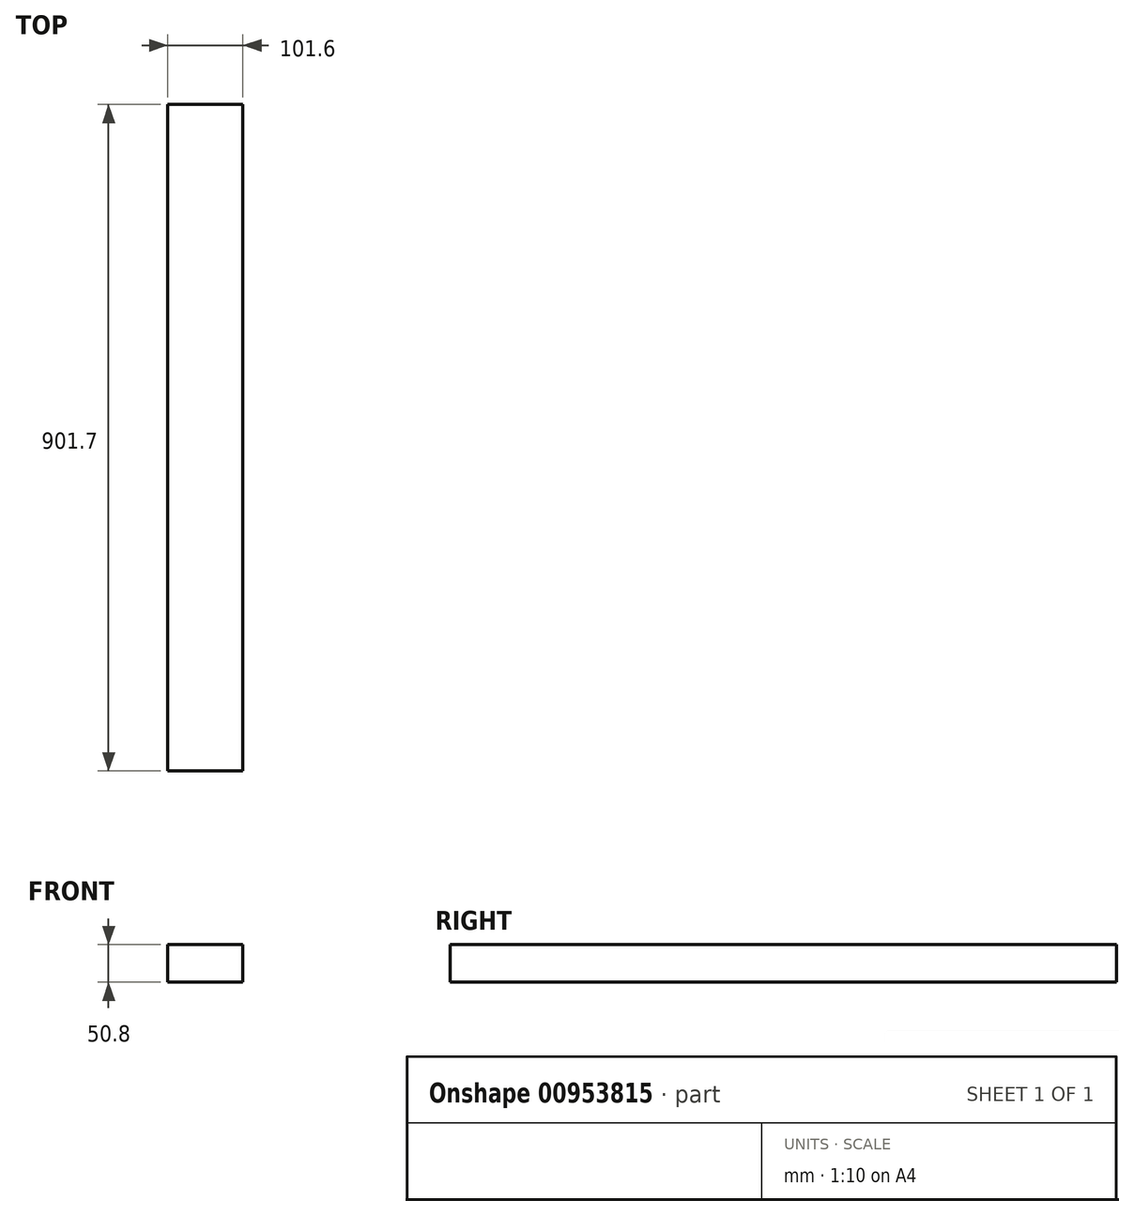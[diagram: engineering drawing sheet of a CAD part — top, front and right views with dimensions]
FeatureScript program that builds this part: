
annotation { "Feature Type Name" : "Feature", "Feature Type Description" : "" }
export const myFeature = defineFeature(function(context is Context, id is Id, definition is map)
    precondition{}
    {
        {
            var Q0;
            Q0=qCreatedBy(makeId("Front.planeOp"),FACE);
            var sketch = newSketch(context, id + "F0", { "sketchPlane" : qUnion([Q0])});
            skLineSegment(sketch, "E0.bottom", {"start": v(-50.8, -25.4) * mm, "end": v(50.8, -25.4) * mm});
            skLineSegment(sketch, "E0.top", {"start": v(-50.8, 25.4) * mm, "end": v(50.8, 25.4) * mm});
            skLineSegment(sketch, "E0.left", {"start": v(-50.8, -25.4) * mm, "end": v(-50.8, 25.4) * mm});
            skLineSegment(sketch, "E0.right", {"start": v(50.8, -25.4) * mm, "end": v(50.8, 25.4) * mm});
            skPoint(sketch, "E0.middle", {"position": v(0, 0) * mm});
            skSolve(sketch);
        }
        {
            var Q0;
            Q0 = qSketchRegion(id + "F0", true);
            extrude(context, id + "F1", {"entities" : qUnion([Q0]), "depth" : 901.7 * mm, "offsetDistance" : 25.4 * mm});
        }
    });
